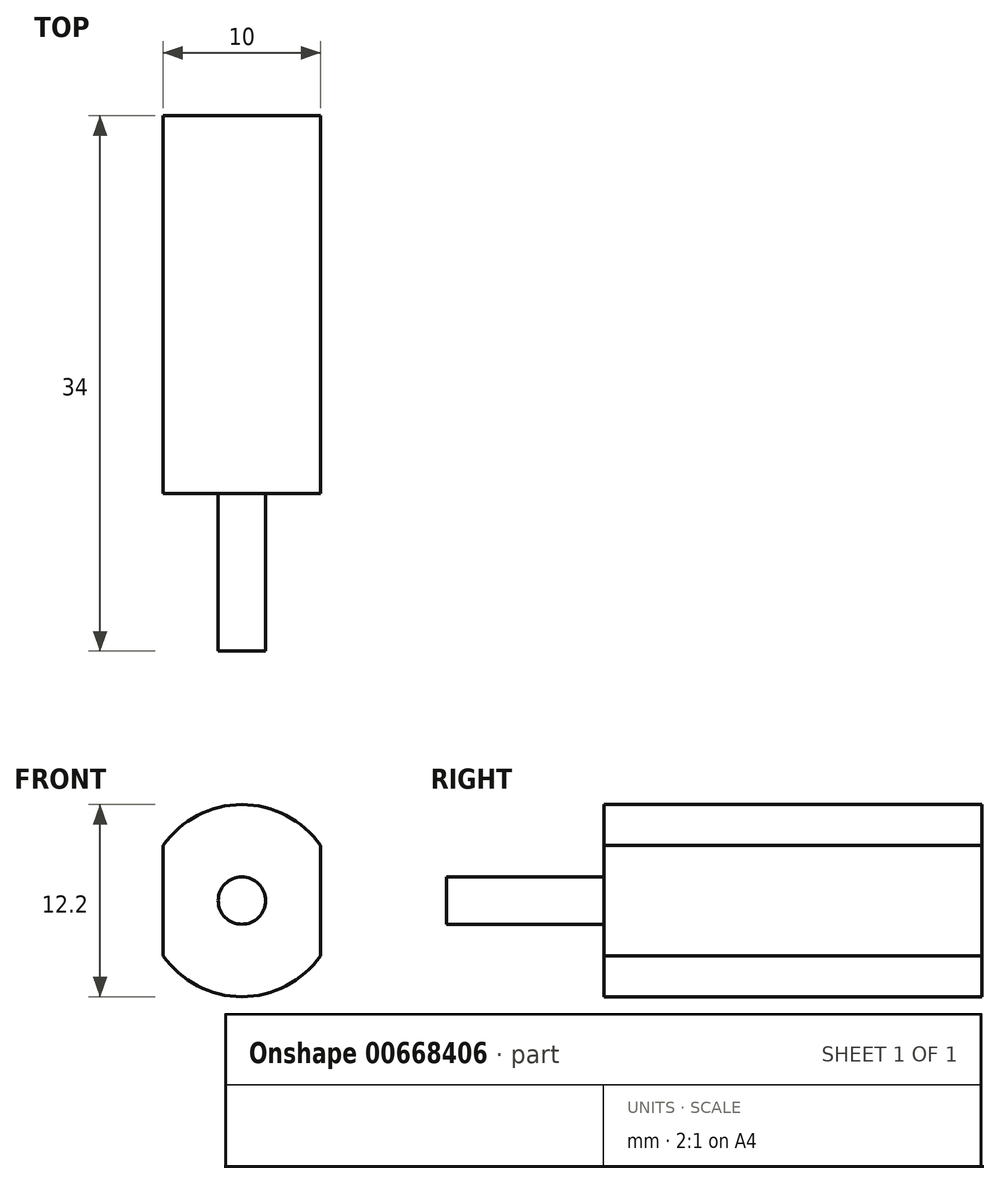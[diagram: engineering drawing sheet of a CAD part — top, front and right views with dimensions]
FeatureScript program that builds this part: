
annotation { "Feature Type Name" : "Feature", "Feature Type Description" : "" }
export const myFeature = defineFeature(function(context is Context, id is Id, definition is map)
    precondition{}
    {
        {
            var Q0;
            Q0=qCreatedBy(makeId("Front.planeOp"),FACE);
            var sketch = newSketch(context, id + "F0", { "sketchPlane" : qUnion([Q0])});
            skLineSegment(sketch, "E0.bottom", {"start": v(0, 0) * mm, "end": v(10, 0) * mm});
            skLineSegment(sketch, "E0.top", {"start": v(0, 7) * mm, "end": v(10, 7) * mm});
            skLineSegment(sketch, "E0.left", {"start": v(0, 0) * mm, "end": v(0, 7) * mm});
            skLineSegment(sketch, "E0.right", {"start": v(10, 0) * mm, "end": v(10, 7) * mm});
            skArc(sketch, "E1", {"start": v(10, 7) * mm, "mid": v(5, 9.6) * mm, "end": v(0, 7) * mm});
            skArc(sketch, "E2", {"start": v(0, 0) * mm, "mid": v(5, -2.6) * mm, "end": v(10, 0) * mm});
            skSolve(sketch);
        }
        {
            var Q0;
            Q0=makeQuery(id+"F0.imprint","IMPRINT",FACE,{"disambiguationData":[TD([[makeQuery(id+"F0.imprint","IMPRINT",EDGE,{"derivedFrom":sQuery(id+"F0.wireOp",EDGE,"E0.bottom")}),-1.0]])]});
            var Q1;
            Q1=makeQuery(id+"F0.imprint","IMPRINT",FACE,{"disambiguationData":[TD([[makeQuery(id+"F0.imprint","IMPRINT",EDGE,{"derivedFrom":sQuery(id+"F0.wireOp",EDGE,"E0.top")}),1.0]])]});
            var Q2;
            Q2=makeQuery(id+"F0.imprint","IMPRINT",FACE,{"disambiguationData":[TD([[makeQuery(id+"F0.imprint","IMPRINT",EDGE,{"derivedFrom":sQuery(id+"F0.wireOp",EDGE,"E0.bottom")}),1.0]])]});
            extrude(context, id + "F1", {"entities" : qUnion([Q0, Q1, Q2]), "depth" : 24 * mm, "offsetDistance" : 25 * mm});
        }
        {
            var Q0;
            Q0=makeQuery(id+"F1.opExtrude","CAP_FACE",FACE,{"disambiguationData":[OSD([sQuery(id+"F0.wireOp",EDGE,"E0.left"),sQuery(id+"F0.wireOp",EDGE,"E0.right"),sQuery(id+"F0.wireOp",EDGE,"E1"),sQuery(id+"F0.wireOp",EDGE,"E2")])],"isStart":false});
            var sketch = newSketch(context, id + "F2", { "sketchPlane" : qUnion([Q0])});
            skCircle(sketch, "E3", {"center": v(5, 3.5) * mm, "radius": 1.5 * mm});
            skSolve(sketch);
        }
        {
            var Q0;
            Q0=makeQuery(id+"F2.imprint","IMPRINT",FACE,{"disambiguationData":[TD([[makeQuery(id+"F2.imprint","IMPRINT",EDGE,{"derivedFrom":sQuery(id+"F2.wireOp",EDGE,"E3")}),1.0]])]});
            extrude(context, id + "F3", {"entities" : qUnion([Q0]), "operationType" : NewBodyOperationType.ADD, "depth" : 10 * mm, "offsetDistance" : 25 * mm});
        }
    });
